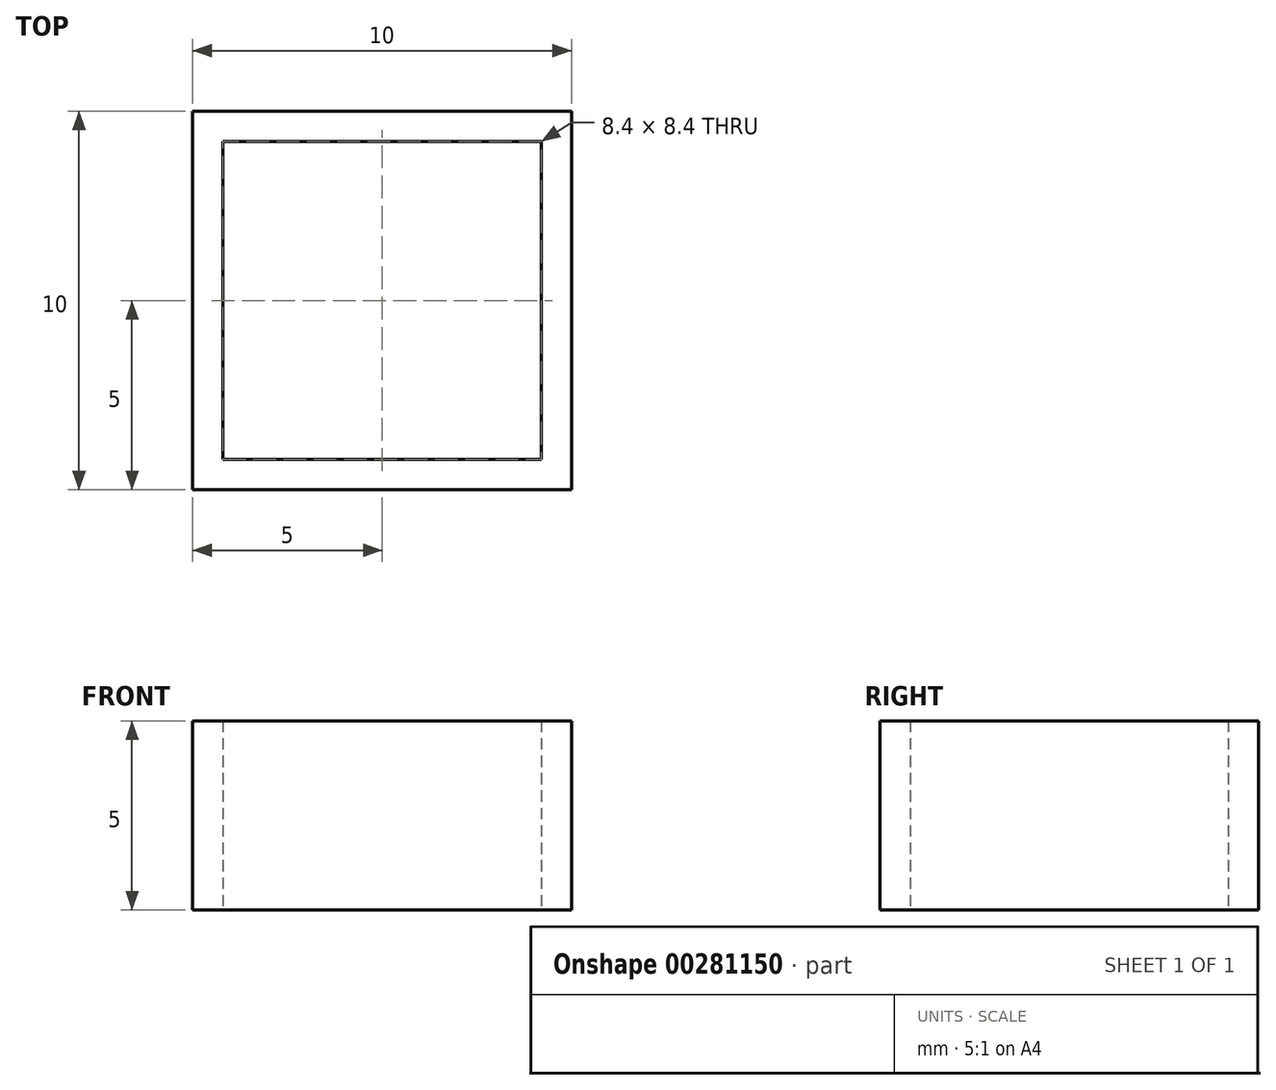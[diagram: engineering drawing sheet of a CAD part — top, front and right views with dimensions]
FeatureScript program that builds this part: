
annotation { "Feature Type Name" : "Feature", "Feature Type Description" : "" }
export const myFeature = defineFeature(function(context is Context, id is Id, definition is map)
    precondition{}
    {
        {
            var Q0;
            Q0=qCreatedBy(makeId("Top.planeOp"),FACE);
            var sketch = newSketch(context, id + "F0", { "sketchPlane" : qUnion([Q0])});
            skLineSegment(sketch, "E0.bottom", {"start": v(5, 5) * mm, "end": v(-5, 5) * mm});
            skLineSegment(sketch, "E0.top", {"start": v(5, -5) * mm, "end": v(-5, -5) * mm});
            skLineSegment(sketch, "E0.left", {"start": v(5, 5) * mm, "end": v(5, -5) * mm});
            skLineSegment(sketch, "E0.right", {"start": v(-5, 5) * mm, "end": v(-5, -5) * mm});
            skPoint(sketch, "E0.middle", {"position": v(0, 0) * mm});
            skLineSegment(sketch, "E1.0", {"start": v(-4.2, 4.2) * mm, "end": v(-4.2, -4.2) * mm});
            skLineSegment(sketch, "E1.1", {"start": v(4.2, 4.2) * mm, "end": v(-4.2, 4.2) * mm});
            skLineSegment(sketch, "E1.2", {"start": v(4.2, 4.2) * mm, "end": v(4.2, -4.2) * mm});
            skLineSegment(sketch, "E1.3", {"start": v(4.2, -4.2) * mm, "end": v(-4.2, -4.2) * mm});
            skSolve(sketch);
        }
        {
            var Q0;
            Q0 = qSketchRegion(id + "F0", true);
            extrude(context, id + "F1", {"entities" : qUnion([Q0]), "depth" : 5 * mm});
        }
    });
